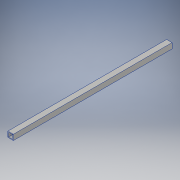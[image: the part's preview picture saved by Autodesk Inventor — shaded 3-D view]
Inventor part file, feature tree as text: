
AUTODESK INVENTOR PART (.ipt)
format: ipt  version: 2018 (Build 220112000, 112)  size: 105,984 bytes
history: native  units: in
note: dims shown in document units (in); Inventor stores cm internally (conversion verified against a paired STEP export)
features: extrude x2, sketch x2
ambient origin geometry x8: Origin, YZ Plane, XZ Plane, XY Plane, X Axis, Y Axis, Z Axis, Center Point
bodies: Solid1 (feature_tree)
feature tree (4):
  extrude  "Extrusion1"  Depth=29.0in
  extrude  "Extrusion2"  Depth=0.125in
  sketch  "Sketch1"  dims[d0=1.0in d1=29.0in]
  sketch  "Sketch2"  dims[d2=1.0in d3=0.0in d4=0.125in d5=0.125in d6=0.75in d7=0.75in d8=29.0in d9=0.0in]
